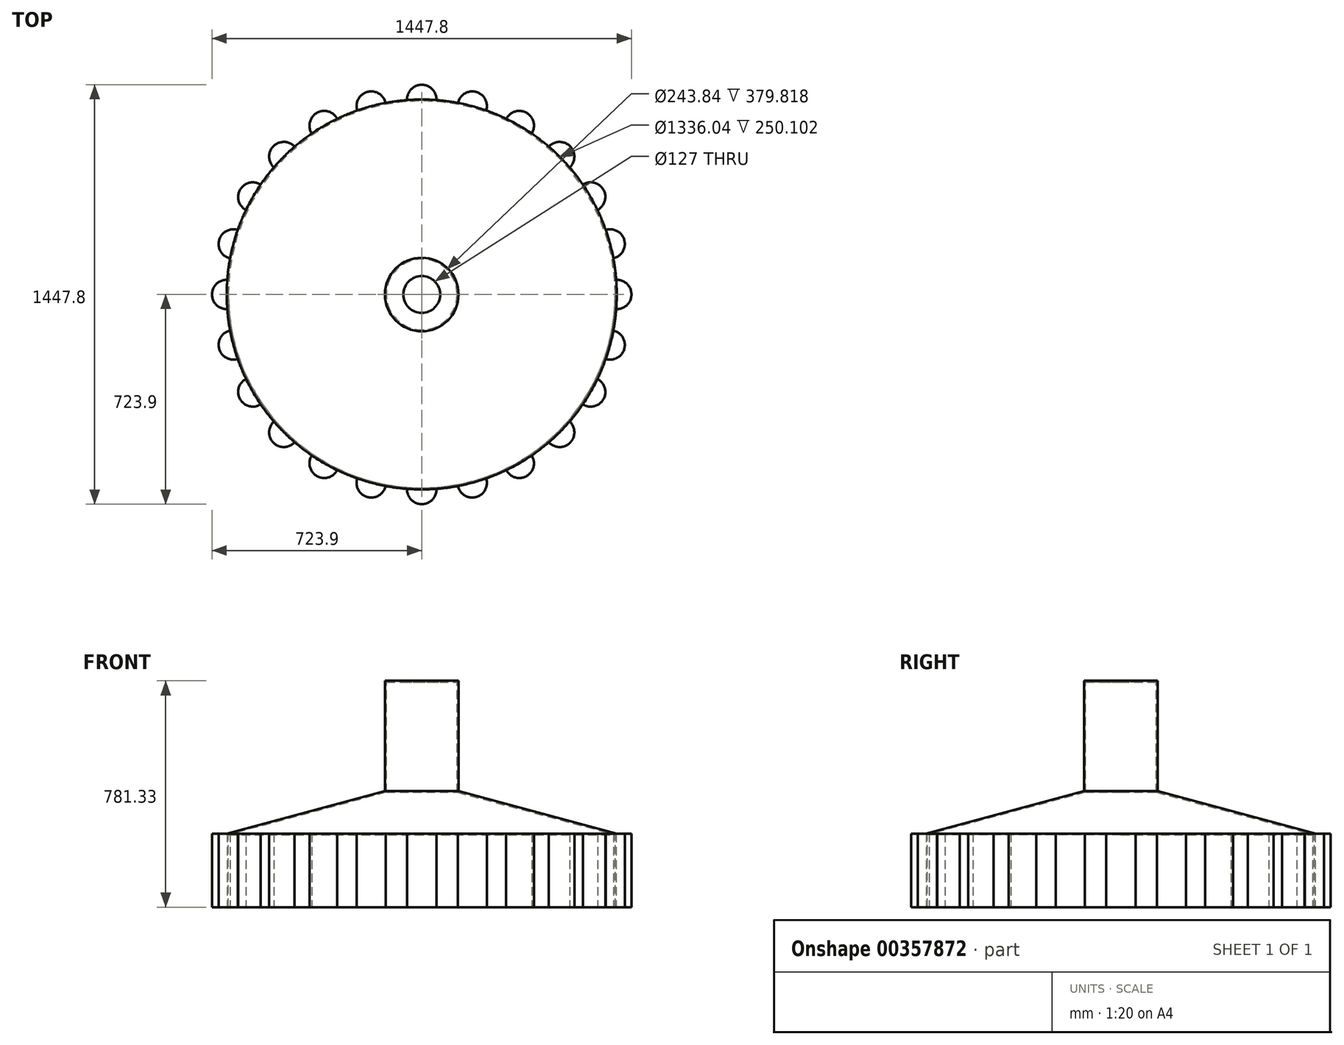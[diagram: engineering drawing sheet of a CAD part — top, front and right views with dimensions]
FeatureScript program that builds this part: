
annotation { "Feature Type Name" : "Feature", "Feature Type Description" : "" }
export const myFeature = defineFeature(function(context is Context, id is Id, definition is map)
    precondition{}
    {
        {
            var Q0;
            Q0=qCreatedBy(makeId("Front.planeOp"),FACE);
            var sketch = newSketch(context, id + "F0", { "sketchPlane" : qUnion([Q0])});
            skLineSegment(sketch, "E0", {"start": v(0, 0) * mm, "end": v(-673.1, 0) * mm});
            skLineSegment(sketch, "E1", {"start": v(-673.1, 0) * mm, "end": v(-673.1, 254) * mm});
            skLineSegment(sketch, "E2", {"start": v(-673.1, 254) * mm, "end": v(-127, 400.33) * mm});
            skLineSegment(sketch, "E3", {"start": v(0, 0) * mm, "end": v(0, 577.47) * mm, "construction": true});
            skLineSegment(sketch, "E4", {"start": v(-127, 400.33) * mm, "end": v(-127, 781.33) * mm});
            skLineSegment(sketch, "E5", {"start": v(-127, 781.33) * mm, "end": v(0, 781.33) * mm});
            skLineSegment(sketch, "E6", {"start": v(0, 781.33) * mm, "end": v(0, 0) * mm});
            skSolve(sketch);
        }
        {
            var Q0;
            Q0=makeQuery(id+"F0.imprint","IMPRINT",FACE,{"disambiguationData":[TD([[makeQuery(id+"F0.imprint","IMPRINT",EDGE,{"derivedFrom":sQuery(id+"F0.wireOp",EDGE,"E0")}),-1.0]])]});
            var Q1;
            Q1=sQuery(id+"F0.wireOp",EDGE,"E6");
            revolve(context, id + "F1", {"entities" : qUnion([Q0]), "axis" : qUnion([Q1]), "revolveType" : RevolveType.FULL});
        }
        {
            var Q0;
            Q0=makeQuery(id+"F1.opRevolve","SWEPT_FACE",FACE,{"disambiguationData":[OSD([sQuery(id+"F0.wireOp",EDGE,"E0")])]});
            shell(context, id + "F2", {"entities" : qUnion([Q0]), "thickness" : 5.08 * mm});
        }
        {
            var Q0;
            Q0=qCreatedBy(makeId("Top.planeOp"),FACE);
            var sketch = newSketch(context, id + "F3", { "sketchPlane" : qUnion([Q0])});
            skCircle(sketch, "E7", {"center": v(0, 0) * mm, "radius": 63.5 * mm});
            skSolve(sketch);
        }
        {
            var Q0;
            Q0=qSketchRegion(id+"F3",true);
            extrude(context, id + "F4", {"entities" : qUnion([Q0]), "operationType" : NewBodyOperationType.REMOVE, "endBound" : BoundingType.THROUGH_ALL, "depth" : 25.4 * mm});
        }
        {
            var Q0;
            Q0=makeQuery(id+"F1.opRevolve","SWEPT_FACE",FACE,{"disambiguationData":[OSD([sQuery(id+"F0.wireOp",EDGE,"E0")])]});
            var sketch = newSketch(context, id + "F5", { "sketchPlane" : qUnion([Q0])});
            skLineSegment(sketch, "E8", {"start": v(-44.13, 0) * mm, "end": v(-818.67, 0) * mm, "construction": true});
            skArc(sketch, "E9", {"start": v(-671.18, 50.76) * mm, "mid": v(-723.9, 0) * mm, "end": v(-671.18, -50.76) * mm});
            skArc(sketch, "E10", {"start": v(-671.18, 50.76) * mm, "mid": v(-673.1, 0) * mm, "end": v(-671.18, -50.76) * mm});
            skSolve(sketch);
        }
        {
            var Q0;
            Q0=makeQuery(id+"F5.imprint","IMPRINT",FACE,{"disambiguationData":[TD([[makeQuery(id+"F5.imprint","IMPRINT",EDGE,{"derivedFrom":sQuery(id+"F5.wireOp",EDGE,"E9")}),1.0]])]});
            extrude(context, id + "F6", {"entities" : qUnion([Q0]), "operationType" : NewBodyOperationType.ADD, "oppositeDirection" : true, "depth" : 254 * mm});
        }
        {
            var Q0;
            Q0=makeQuery(id+"F1.opRevolve","SWEPT_BODY",BODY,{"disambiguationData":[OSD([sQuery(id+"F0.wireOp",EDGE,"E0"),sQuery(id+"F0.wireOp",EDGE,"E1"),sQuery(id+"F0.wireOp",EDGE,"E2"),sQuery(id+"F0.wireOp",EDGE,"E4"),sQuery(id+"F0.wireOp",EDGE,"E5"),sQuery(id+"F0.wireOp",EDGE,"E6")])]});
            var Q1;
            Q1=makeQuery(id+"F4.boolean.opBoolean","INTERSECT",EDGE,{"derivedFrom":[makeQuery(id+"F1.opRevolve","SWEPT_FACE",FACE,{"disambiguationData":[OSD([sQuery(id+"F0.wireOp",EDGE,"E5")])]}),makeQuery(id+"F4.opExtrude","SWEPT_FACE",FACE,{"disambiguationData":[OSD([sQuery(id+"F3.wireOp",EDGE,"E7")])]})]});
            circularPattern(context, id + "F7", {"operationType" : NewBodyOperationType.ADD, "entities" : qUnion([Q0]), "axis" : qUnion([Q1]), "angle" : 360 * degree, "instanceCount" : 24, "equalSpace" : true});
        }
    });
